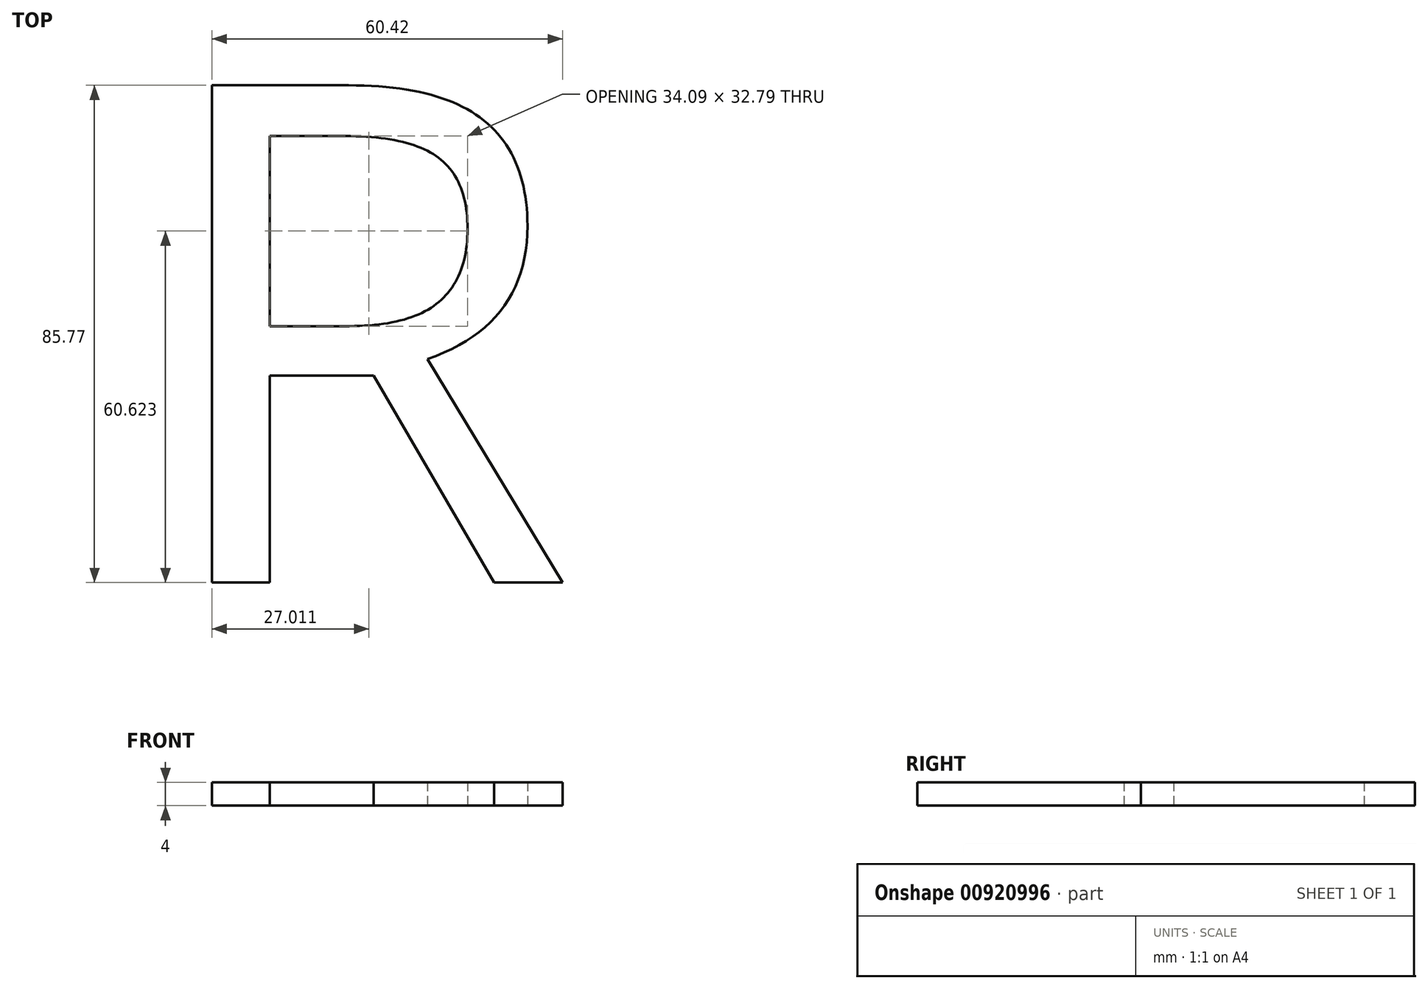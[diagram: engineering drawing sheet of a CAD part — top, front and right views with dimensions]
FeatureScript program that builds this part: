
annotation { "Feature Type Name" : "Feature", "Feature Type Description" : "" }
export const myFeature = defineFeature(function(context is Context, id is Id, definition is map)
    precondition{}
    {
        {
            var Q0;
            Q0=qCreatedBy(makeId("Top.planeOp"),FACE);
            var sketch = newSketch(context, id + "F0", { "sketchPlane" : qUnion([Q0])});
            skText(sketch, "E0", { "text": "R", "fontName": "OpenSans-Regular.ttf"});
            const initialGuessF0  = {"E0": [-0.03414, -0.04928, 1, 0, 0.0865]};
            skSetInitialGuess(sketch, initialGuessF0);
            skSolve(sketch);
        }
        {
            var Q0;
            Q0=makeQuery(id+"F0.imprint","IMPRINT",FACE,{"disambiguationData":[TD([[makeQuery(id+"F0.imprint","IMPRINT",EDGE,{"derivedFrom":sQuery(id+"F0.wireOp",EDGE,"E0.sketch_text.stroke-0")}),-1.0]])]});
            extrude(context, id + "F1", {"entities" : qUnion([Q0]), "depth" : 4 * mm, "offsetDistance" : 25 * mm});
        }
    });
